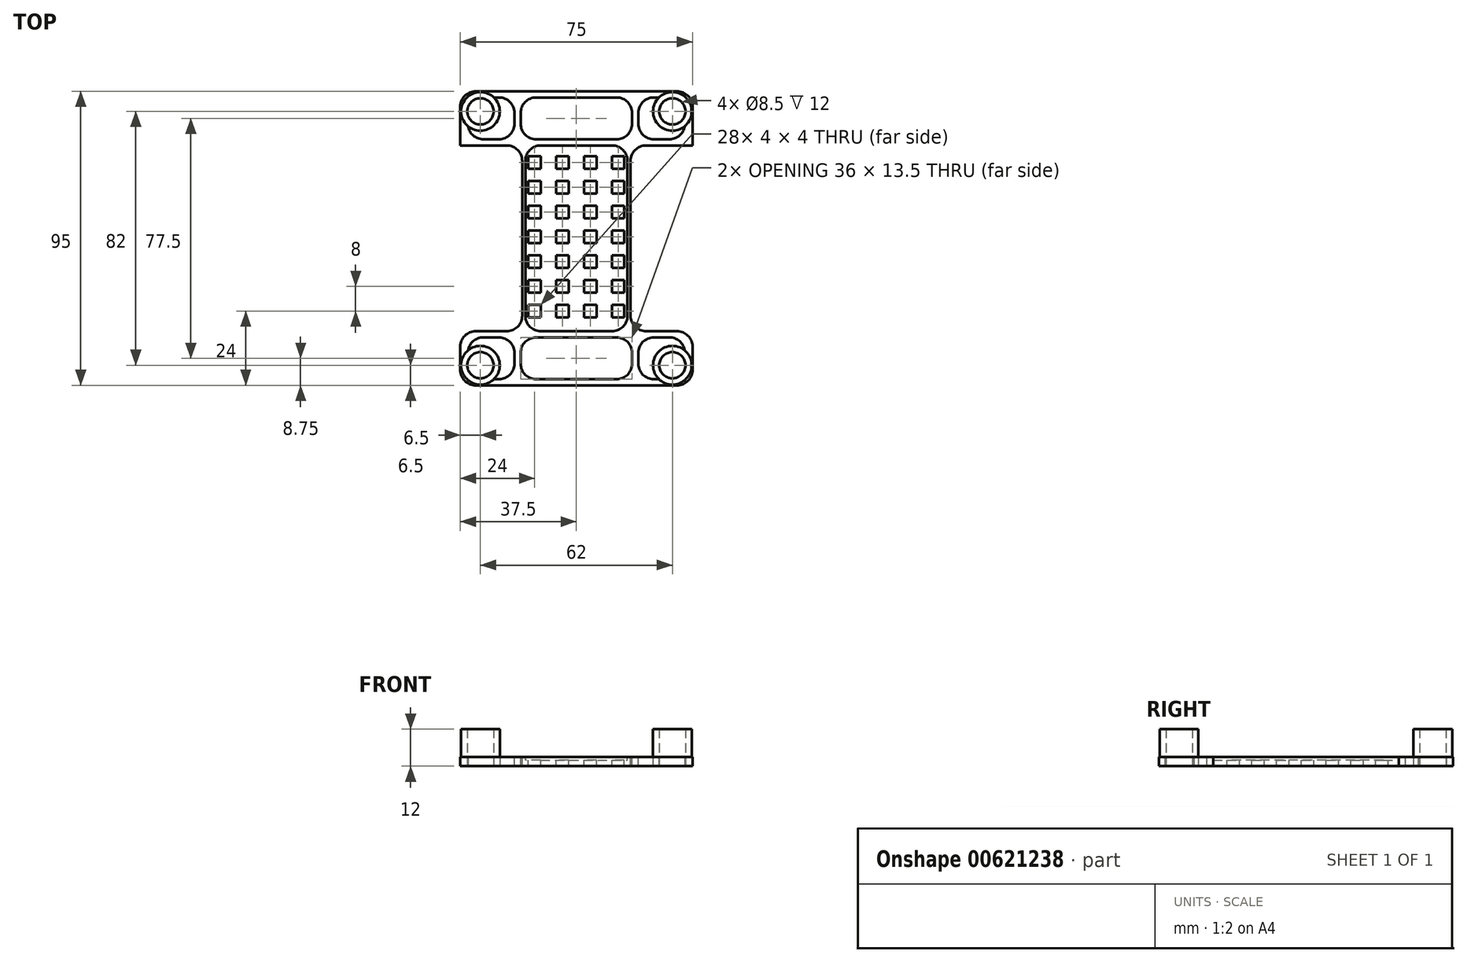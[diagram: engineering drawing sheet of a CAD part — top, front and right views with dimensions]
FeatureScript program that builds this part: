
annotation { "Feature Type Name" : "Feature", "Feature Type Description" : "" }
export const myFeature = defineFeature(function(context is Context, id is Id, definition is map)
    precondition{}
    {
        {
            var Q0;
            Q0=qCreatedBy(makeId("Top.planeOp"),FACE);
            var sketch = newSketch(context, id + "F0", { "sketchPlane" : qUnion([Q0])});
            skLineSegment(sketch, "E0.bottom", {"start": v(-37.5, 47.5) * mm, "end": v(37.5, 47.5) * mm});
            skLineSegment(sketch, "E0.top", {"start": v(-37.5, -47.5) * mm, "end": v(37.5, -47.5) * mm});
            skLineSegment(sketch, "E0.left", {"start": v(-37.5, 47.5) * mm, "end": v(-37.5, -47.5) * mm});
            skLineSegment(sketch, "E0.right", {"start": v(37.5, 47.5) * mm, "end": v(37.5, -47.5) * mm});
            skPoint(sketch, "E0.middle", {"position": v(0, 0) * mm});
            skSolve(sketch);
        }
        {
            var Q0;
            Q0=makeQuery(id+"F0.imprint","IMPRINT",FACE,{"disambiguationData":[TD([[makeQuery(id+"F0.imprint","IMPRINT",EDGE,{"derivedFrom":sQuery(id+"F0.wireOp",EDGE,"E0.bottom")}),-1.0]])]});
            extrude(context, id + "F1", {"entities" : qUnion([Q0]), "depth" : 3 * mm, "offsetDistance" : 25 * mm});
        }
        {
            var Q0;
            Q0=makeQuery(id+"F1.opExtrude","CAP_FACE",FACE,{"disambiguationData":[OSD([sQuery(id+"F0.wireOp",EDGE,"E0.bottom"),sQuery(id+"F0.wireOp",EDGE,"E0.top"),sQuery(id+"F0.wireOp",EDGE,"E0.left"),sQuery(id+"F0.wireOp",EDGE,"E0.right")])],"isStart":false});
            var sketch = newSketch(context, id + "F2", { "sketchPlane" : qUnion([Q0])});
            skLineSegment(sketch, "E1.bottom", {"start": v(-37.5, 30) * mm, "end": v(-17.5, 30) * mm});
            skLineSegment(sketch, "E1.top", {"start": v(-37.5, -30) * mm, "end": v(-17.5, -30) * mm});
            skLineSegment(sketch, "E1.left", {"start": v(-37.5, 30) * mm, "end": v(-37.5, -30) * mm});
            skLineSegment(sketch, "E1.right", {"start": v(-17.5, 30) * mm, "end": v(-17.5, -30) * mm});
            skLineSegment(sketch, "E2.bottom", {"start": v(37.5, 30) * mm, "end": v(17.5, 30) * mm});
            skLineSegment(sketch, "E2.top", {"start": v(37.5, -30) * mm, "end": v(17.5, -30) * mm});
            skLineSegment(sketch, "E2.left", {"start": v(37.5, 30) * mm, "end": v(37.5, -30) * mm});
            skLineSegment(sketch, "E2.right", {"start": v(17.5, 30) * mm, "end": v(17.5, -30) * mm});
            skSolve(sketch);
        }
        {
            var Q0;
            Q0=makeQuery(id+"F2.imprint","IMPRINT",FACE,{"disambiguationData":[TD([[makeQuery(id+"F2.imprint","IMPRINT",EDGE,{"derivedFrom":sQuery(id+"F2.wireOp",EDGE,"E1.bottom")}),-1.0]])]});
            var Q1;
            Q1=makeQuery(id+"F2.imprint","IMPRINT",FACE,{"disambiguationData":[TD([[makeQuery(id+"F2.imprint","IMPRINT",EDGE,{"derivedFrom":sQuery(id+"F2.wireOp",EDGE,"E2.bottom")}),1.0]])]});
            extrude(context, id + "F3", {"entities" : qUnion([Q0, Q1]), "operationType" : NewBodyOperationType.REMOVE, "endBound" : BoundingType.THROUGH_ALL, "oppositeDirection" : true, "depth" : 25 * mm, "offsetDistance" : 25 * mm});
        }
        {
            var Q0;
            Q0=makeQuery(id+"F1.opExtrude","CAP_FACE",FACE,{"disambiguationData":[OSD([sQuery(id+"F0.wireOp",EDGE,"E0.bottom"),sQuery(id+"F0.wireOp",EDGE,"E0.top"),sQuery(id+"F0.wireOp",EDGE,"E0.left"),sQuery(id+"F0.wireOp",EDGE,"E0.right")])],"isStart":false});
            var sketch = newSketch(context, id + "F4", { "sketchPlane" : qUnion([Q0])});
            skLineSegment(sketch, "E3.bottom", {"start": v(-11.5, 22.5) * mm, "end": v(-15.5, 22.5) * mm});
            skLineSegment(sketch, "E3.top", {"start": v(-11.5, 26.5) * mm, "end": v(-15.5, 26.5) * mm});
            skLineSegment(sketch, "E3.left", {"start": v(-11.5, 22.5) * mm, "end": v(-11.5, 26.5) * mm});
            skLineSegment(sketch, "E3.right", {"start": v(-15.5, 22.5) * mm, "end": v(-15.5, 26.5) * mm});
            skPoint(sketch, "E3.middle", {"position": v(-13.5, 24.5) * mm});
            skLineSegment(sketch, "E4.0.1.0", {"start": v(-11.5, 14.5) * mm, "end": v(-11.5, 18.5) * mm});
            skLineSegment(sketch, "E4.0.1.1", {"start": v(-11.5, 14.5) * mm, "end": v(-15.5, 14.5) * mm});
            skLineSegment(sketch, "E4.0.1.2", {"start": v(-11.5, 18.5) * mm, "end": v(-15.5, 18.5) * mm});
            skPoint(sketch, "E4.0.1.3", {"position": v(-13.5, 16.5) * mm});
            skLineSegment(sketch, "E4.0.1.4", {"start": v(-15.5, 14.5) * mm, "end": v(-15.5, 18.5) * mm});
            skLineSegment(sketch, "E4.0.2.0", {"start": v(-11.5, 6.5) * mm, "end": v(-11.5, 10.5) * mm});
            skLineSegment(sketch, "E4.0.2.1", {"start": v(-11.5, 6.5) * mm, "end": v(-15.5, 6.5) * mm});
            skLineSegment(sketch, "E4.0.2.2", {"start": v(-11.5, 10.5) * mm, "end": v(-15.5, 10.5) * mm});
            skPoint(sketch, "E4.0.2.3", {"position": v(-13.5, 8.5) * mm});
            skLineSegment(sketch, "E4.0.2.4", {"start": v(-15.5, 6.5) * mm, "end": v(-15.5, 10.5) * mm});
            skLineSegment(sketch, "E4.0.3.0", {"start": v(-11.5, -1.5) * mm, "end": v(-11.5, 2.5) * mm});
            skLineSegment(sketch, "E4.0.3.1", {"start": v(-11.5, -1.5) * mm, "end": v(-15.5, -1.5) * mm});
            skLineSegment(sketch, "E4.0.3.2", {"start": v(-11.5, 2.5) * mm, "end": v(-15.5, 2.5) * mm});
            skPoint(sketch, "E4.0.3.3", {"position": v(-13.5, 0.5) * mm});
            skLineSegment(sketch, "E4.0.3.4", {"start": v(-15.5, -1.5) * mm, "end": v(-15.5, 2.5) * mm});
            skLineSegment(sketch, "E4.1.0.0", {"start": v(-2.5, 22.5) * mm, "end": v(-2.5, 26.5) * mm});
            skLineSegment(sketch, "E4.1.0.1", {"start": v(-2.5, 22.5) * mm, "end": v(-6.5, 22.5) * mm});
            skLineSegment(sketch, "E4.1.0.2", {"start": v(-2.5, 26.5) * mm, "end": v(-6.5, 26.5) * mm});
            skPoint(sketch, "E4.1.0.3", {"position": v(-4.5, 24.5) * mm});
            skLineSegment(sketch, "E4.1.0.4", {"start": v(-6.5, 22.5) * mm, "end": v(-6.5, 26.5) * mm});
            skLineSegment(sketch, "E4.1.1.0", {"start": v(-2.5, 14.5) * mm, "end": v(-2.5, 18.5) * mm});
            skLineSegment(sketch, "E4.1.1.1", {"start": v(-2.5, 14.5) * mm, "end": v(-6.5, 14.5) * mm});
            skLineSegment(sketch, "E4.1.1.2", {"start": v(-2.5, 18.5) * mm, "end": v(-6.5, 18.5) * mm});
            skPoint(sketch, "E4.1.1.3", {"position": v(-4.5, 16.5) * mm});
            skLineSegment(sketch, "E4.1.1.4", {"start": v(-6.5, 14.5) * mm, "end": v(-6.5, 18.5) * mm});
            skLineSegment(sketch, "E4.1.2.0", {"start": v(-2.5, 6.5) * mm, "end": v(-2.5, 10.5) * mm});
            skLineSegment(sketch, "E4.1.2.1", {"start": v(-2.5, 6.5) * mm, "end": v(-6.5, 6.5) * mm});
            skLineSegment(sketch, "E4.1.2.2", {"start": v(-2.5, 10.5) * mm, "end": v(-6.5, 10.5) * mm});
            skPoint(sketch, "E4.1.2.3", {"position": v(-4.5, 8.5) * mm});
            skLineSegment(sketch, "E4.1.2.4", {"start": v(-6.5, 6.5) * mm, "end": v(-6.5, 10.5) * mm});
            skLineSegment(sketch, "E4.1.3.0", {"start": v(-2.5, -1.5) * mm, "end": v(-2.5, 2.5) * mm});
            skLineSegment(sketch, "E4.1.3.1", {"start": v(-2.5, -1.5) * mm, "end": v(-6.5, -1.5) * mm});
            skLineSegment(sketch, "E4.1.3.2", {"start": v(-2.5, 2.5) * mm, "end": v(-6.5, 2.5) * mm});
            skPoint(sketch, "E4.1.3.3", {"position": v(-4.5, 0.5) * mm});
            skLineSegment(sketch, "E4.1.3.4", {"start": v(-6.5, -1.5) * mm, "end": v(-6.5, 2.5) * mm});
            skLineSegment(sketch, "E4.2.0.0", {"start": v(6.5, 22.5) * mm, "end": v(6.5, 26.5) * mm});
            skLineSegment(sketch, "E4.2.0.1", {"start": v(6.5, 22.5) * mm, "end": v(2.5, 22.5) * mm});
            skLineSegment(sketch, "E4.2.0.2", {"start": v(6.5, 26.5) * mm, "end": v(2.5, 26.5) * mm});
            skPoint(sketch, "E4.2.0.3", {"position": v(4.5, 24.5) * mm});
            skLineSegment(sketch, "E4.2.0.4", {"start": v(2.5, 22.5) * mm, "end": v(2.5, 26.5) * mm});
            skLineSegment(sketch, "E4.2.1.0", {"start": v(6.5, 14.5) * mm, "end": v(6.5, 18.5) * mm});
            skLineSegment(sketch, "E4.2.1.1", {"start": v(6.5, 14.5) * mm, "end": v(2.5, 14.5) * mm});
            skLineSegment(sketch, "E4.2.1.2", {"start": v(6.5, 18.5) * mm, "end": v(2.5, 18.5) * mm});
            skPoint(sketch, "E4.2.1.3", {"position": v(4.5, 16.5) * mm});
            skLineSegment(sketch, "E4.2.1.4", {"start": v(2.5, 14.5) * mm, "end": v(2.5, 18.5) * mm});
            skLineSegment(sketch, "E4.2.2.0", {"start": v(6.5, 6.5) * mm, "end": v(6.5, 10.5) * mm});
            skLineSegment(sketch, "E4.2.2.1", {"start": v(6.5, 6.5) * mm, "end": v(2.5, 6.5) * mm});
            skLineSegment(sketch, "E4.2.2.2", {"start": v(6.5, 10.5) * mm, "end": v(2.5, 10.5) * mm});
            skPoint(sketch, "E4.2.2.3", {"position": v(4.5, 8.5) * mm});
            skLineSegment(sketch, "E4.2.2.4", {"start": v(2.5, 6.5) * mm, "end": v(2.5, 10.5) * mm});
            skLineSegment(sketch, "E4.2.3.0", {"start": v(6.5, -1.5) * mm, "end": v(6.5, 2.5) * mm});
            skLineSegment(sketch, "E4.2.3.1", {"start": v(6.5, -1.5) * mm, "end": v(2.5, -1.5) * mm});
            skLineSegment(sketch, "E4.2.3.2", {"start": v(6.5, 2.5) * mm, "end": v(2.5, 2.5) * mm});
            skPoint(sketch, "E4.2.3.3", {"position": v(4.5, 0.5) * mm});
            skLineSegment(sketch, "E4.2.3.4", {"start": v(2.5, -1.5) * mm, "end": v(2.5, 2.5) * mm});
            skLineSegment(sketch, "E4.direction1", {"start": v(-15.5, 22.5) * mm, "end": v(-6.5, 22.5) * mm, "construction": true});
            skLineSegment(sketch, "E4.direction2", {"start": v(-15.5, 22.5) * mm, "end": v(-15.5, 14.5) * mm, "construction": true});
            skLineSegment(sketch, "E5.0.3.0", {"start": v(15.5, 22.5) * mm, "end": v(15.5, 26.5) * mm});
            skLineSegment(sketch, "E5.3.3.0", {"start": v(15.5, 22.5) * mm, "end": v(11.5, 22.5) * mm});
            skLineSegment(sketch, "E5.6.3.0", {"start": v(15.5, 26.5) * mm, "end": v(11.5, 26.5) * mm});
            skPoint(sketch, "E5.9.3.0", {"position": v(13.5, 24.5) * mm});
            skLineSegment(sketch, "E5.10.3.0", {"start": v(11.5, 22.5) * mm, "end": v(11.5, 26.5) * mm});
            skLineSegment(sketch, "E5.0.3.1", {"start": v(15.5, 14.5) * mm, "end": v(15.5, 18.5) * mm});
            skLineSegment(sketch, "E5.3.3.1", {"start": v(15.5, 14.5) * mm, "end": v(11.5, 14.5) * mm});
            skLineSegment(sketch, "E5.6.3.1", {"start": v(15.5, 18.5) * mm, "end": v(11.5, 18.5) * mm});
            skPoint(sketch, "E5.9.3.1", {"position": v(13.5, 16.5) * mm});
            skLineSegment(sketch, "E5.10.3.1", {"start": v(11.5, 14.5) * mm, "end": v(11.5, 18.5) * mm});
            skLineSegment(sketch, "E5.0.3.2", {"start": v(15.5, 6.5) * mm, "end": v(15.5, 10.5) * mm});
            skLineSegment(sketch, "E5.3.3.2", {"start": v(15.5, 6.5) * mm, "end": v(11.5, 6.5) * mm});
            skLineSegment(sketch, "E5.6.3.2", {"start": v(15.5, 10.5) * mm, "end": v(11.5, 10.5) * mm});
            skPoint(sketch, "E5.9.3.2", {"position": v(13.5, 8.5) * mm});
            skLineSegment(sketch, "E5.10.3.2", {"start": v(11.5, 6.5) * mm, "end": v(11.5, 10.5) * mm});
            skLineSegment(sketch, "E5.0.3.3", {"start": v(15.5, -1.5) * mm, "end": v(15.5, 2.5) * mm});
            skLineSegment(sketch, "E5.3.3.3", {"start": v(15.5, -1.5) * mm, "end": v(11.5, -1.5) * mm});
            skLineSegment(sketch, "E5.6.3.3", {"start": v(15.5, 2.5) * mm, "end": v(11.5, 2.5) * mm});
            skPoint(sketch, "E5.9.3.3", {"position": v(13.5, 0.5) * mm});
            skLineSegment(sketch, "E5.10.3.3", {"start": v(11.5, -1.5) * mm, "end": v(11.5, 2.5) * mm});
            skLineSegment(sketch, "E6.0.0.4", {"start": v(-11.5, -9.5) * mm, "end": v(-11.5, -5.5) * mm});
            skLineSegment(sketch, "E6.3.0.4", {"start": v(-11.5, -9.5) * mm, "end": v(-15.5, -9.5) * mm});
            skLineSegment(sketch, "E6.6.0.4", {"start": v(-11.5, -5.5) * mm, "end": v(-15.5, -5.5) * mm});
            skPoint(sketch, "E6.9.0.4", {"position": v(-13.5, -7.5) * mm});
            skLineSegment(sketch, "E6.10.0.4", {"start": v(-15.5, -9.5) * mm, "end": v(-15.5, -5.5) * mm});
            skLineSegment(sketch, "E6.0.0.5", {"start": v(-11.5, -17.5) * mm, "end": v(-11.5, -13.5) * mm});
            skLineSegment(sketch, "E6.3.0.5", {"start": v(-11.5, -17.5) * mm, "end": v(-15.5, -17.5) * mm});
            skLineSegment(sketch, "E6.6.0.5", {"start": v(-11.5, -13.5) * mm, "end": v(-15.5, -13.5) * mm});
            skPoint(sketch, "E6.9.0.5", {"position": v(-13.5, -15.5) * mm});
            skLineSegment(sketch, "E6.10.0.5", {"start": v(-15.5, -17.5) * mm, "end": v(-15.5, -13.5) * mm});
            skLineSegment(sketch, "E6.0.1.4", {"start": v(-2.5, -9.5) * mm, "end": v(-2.5, -5.5) * mm});
            skLineSegment(sketch, "E6.3.1.4", {"start": v(-2.5, -9.5) * mm, "end": v(-6.5, -9.5) * mm});
            skLineSegment(sketch, "E6.6.1.4", {"start": v(-2.5, -5.5) * mm, "end": v(-6.5, -5.5) * mm});
            skPoint(sketch, "E6.9.1.4", {"position": v(-4.5, -7.5) * mm});
            skLineSegment(sketch, "E6.10.1.4", {"start": v(-6.5, -9.5) * mm, "end": v(-6.5, -5.5) * mm});
            skLineSegment(sketch, "E6.0.1.5", {"start": v(-2.5, -17.5) * mm, "end": v(-2.5, -13.5) * mm});
            skLineSegment(sketch, "E6.3.1.5", {"start": v(-2.5, -17.5) * mm, "end": v(-6.5, -17.5) * mm});
            skLineSegment(sketch, "E6.6.1.5", {"start": v(-2.5, -13.5) * mm, "end": v(-6.5, -13.5) * mm});
            skPoint(sketch, "E6.9.1.5", {"position": v(-4.5, -15.5) * mm});
            skLineSegment(sketch, "E6.10.1.5", {"start": v(-6.5, -17.5) * mm, "end": v(-6.5, -13.5) * mm});
            skLineSegment(sketch, "E6.0.2.4", {"start": v(6.5, -9.5) * mm, "end": v(6.5, -5.5) * mm});
            skLineSegment(sketch, "E6.3.2.4", {"start": v(6.5, -9.5) * mm, "end": v(2.5, -9.5) * mm});
            skLineSegment(sketch, "E6.6.2.4", {"start": v(6.5, -5.5) * mm, "end": v(2.5, -5.5) * mm});
            skPoint(sketch, "E6.9.2.4", {"position": v(4.5, -7.5) * mm});
            skLineSegment(sketch, "E6.10.2.4", {"start": v(2.5, -9.5) * mm, "end": v(2.5, -5.5) * mm});
            skLineSegment(sketch, "E6.0.2.5", {"start": v(6.5, -17.5) * mm, "end": v(6.5, -13.5) * mm});
            skLineSegment(sketch, "E6.3.2.5", {"start": v(6.5, -17.5) * mm, "end": v(2.5, -17.5) * mm});
            skLineSegment(sketch, "E6.6.2.5", {"start": v(6.5, -13.5) * mm, "end": v(2.5, -13.5) * mm});
            skPoint(sketch, "E6.9.2.5", {"position": v(4.5, -15.5) * mm});
            skLineSegment(sketch, "E6.10.2.5", {"start": v(2.5, -17.5) * mm, "end": v(2.5, -13.5) * mm});
            skLineSegment(sketch, "E6.0.3.4", {"start": v(15.5, -9.5) * mm, "end": v(15.5, -5.5) * mm});
            skLineSegment(sketch, "E6.3.3.4", {"start": v(15.5, -9.5) * mm, "end": v(11.5, -9.5) * mm});
            skLineSegment(sketch, "E6.6.3.4", {"start": v(15.5, -5.5) * mm, "end": v(11.5, -5.5) * mm});
            skPoint(sketch, "E6.9.3.4", {"position": v(13.5, -7.5) * mm});
            skLineSegment(sketch, "E6.10.3.4", {"start": v(11.5, -9.5) * mm, "end": v(11.5, -5.5) * mm});
            skLineSegment(sketch, "E6.0.3.5", {"start": v(15.5, -17.5) * mm, "end": v(15.5, -13.5) * mm});
            skLineSegment(sketch, "E6.3.3.5", {"start": v(15.5, -17.5) * mm, "end": v(11.5, -17.5) * mm});
            skLineSegment(sketch, "E6.6.3.5", {"start": v(15.5, -13.5) * mm, "end": v(11.5, -13.5) * mm});
            skPoint(sketch, "E6.9.3.5", {"position": v(13.5, -15.5) * mm});
            skLineSegment(sketch, "E6.10.3.5", {"start": v(11.5, -17.5) * mm, "end": v(11.5, -13.5) * mm});
            skLineSegment(sketch, "E7.0.0.6", {"start": v(-11.5, -25.5) * mm, "end": v(-11.5, -21.5) * mm});
            skLineSegment(sketch, "E7.3.0.6", {"start": v(-11.5, -25.5) * mm, "end": v(-15.5, -25.5) * mm});
            skLineSegment(sketch, "E7.6.0.6", {"start": v(-11.5, -21.5) * mm, "end": v(-15.5, -21.5) * mm});
            skPoint(sketch, "E7.9.0.6", {"position": v(-13.5, -23.5) * mm});
            skLineSegment(sketch, "E7.10.0.6", {"start": v(-15.5, -25.5) * mm, "end": v(-15.5, -21.5) * mm});
            skLineSegment(sketch, "E7.0.1.6", {"start": v(-2.5, -25.5) * mm, "end": v(-2.5, -21.5) * mm});
            skLineSegment(sketch, "E7.3.1.6", {"start": v(-2.5, -25.5) * mm, "end": v(-6.5, -25.5) * mm});
            skLineSegment(sketch, "E7.6.1.6", {"start": v(-2.5, -21.5) * mm, "end": v(-6.5, -21.5) * mm});
            skPoint(sketch, "E7.9.1.6", {"position": v(-4.5, -23.5) * mm});
            skLineSegment(sketch, "E7.10.1.6", {"start": v(-6.5, -25.5) * mm, "end": v(-6.5, -21.5) * mm});
            skLineSegment(sketch, "E7.0.2.6", {"start": v(6.5, -25.5) * mm, "end": v(6.5, -21.5) * mm});
            skLineSegment(sketch, "E7.3.2.6", {"start": v(6.5, -25.5) * mm, "end": v(2.5, -25.5) * mm});
            skLineSegment(sketch, "E7.6.2.6", {"start": v(6.5, -21.5) * mm, "end": v(2.5, -21.5) * mm});
            skPoint(sketch, "E7.9.2.6", {"position": v(4.5, -23.5) * mm});
            skLineSegment(sketch, "E7.10.2.6", {"start": v(2.5, -25.5) * mm, "end": v(2.5, -21.5) * mm});
            skLineSegment(sketch, "E7.0.3.6", {"start": v(15.5, -25.5) * mm, "end": v(15.5, -21.5) * mm});
            skLineSegment(sketch, "E7.3.3.6", {"start": v(15.5, -25.5) * mm, "end": v(11.5, -25.5) * mm});
            skLineSegment(sketch, "E7.6.3.6", {"start": v(15.5, -21.5) * mm, "end": v(11.5, -21.5) * mm});
            skPoint(sketch, "E7.9.3.6", {"position": v(13.5, -23.5) * mm});
            skLineSegment(sketch, "E7.10.3.6", {"start": v(11.5, -25.5) * mm, "end": v(11.5, -21.5) * mm});
            skSolve(sketch);
        }
        {
            var Q0;
            Q0=makeQuery(id+"F4.imprint","IMPRINT",FACE,{"disambiguationData":[TD([[makeQuery(id+"F4.imprint","IMPRINT",EDGE,{"derivedFrom":sQuery(id+"F4.wireOp",EDGE,"E5.0.3.3")}),1.0]])]});
            var Q1;
            Q1=makeQuery(id+"F4.imprint","IMPRINT",FACE,{"disambiguationData":[TD([[makeQuery(id+"F4.imprint","IMPRINT",EDGE,{"derivedFrom":sQuery(id+"F4.wireOp",EDGE,"E5.0.3.1")}),1.0]])]});
            var Q2;
            Q2=makeQuery(id+"F4.imprint","IMPRINT",FACE,{"disambiguationData":[TD([[makeQuery(id+"F4.imprint","IMPRINT",EDGE,{"derivedFrom":sQuery(id+"F4.wireOp",EDGE,"E5.0.3.2")}),1.0]])]});
            var Q3;
            Q3=makeQuery(id+"F4.imprint","IMPRINT",FACE,{"disambiguationData":[TD([[makeQuery(id+"F4.imprint","IMPRINT",EDGE,{"derivedFrom":sQuery(id+"F4.wireOp",EDGE,"E3.bottom")}),-1.0]])]});
            var Q4;
            Q4=makeQuery(id+"F4.imprint","IMPRINT",FACE,{"disambiguationData":[TD([[makeQuery(id+"F4.imprint","IMPRINT",EDGE,{"derivedFrom":sQuery(id+"F4.wireOp",EDGE,"E4.0.1.0")}),1.0]])]});
            var Q5;
            Q5=makeQuery(id+"F4.imprint","IMPRINT",FACE,{"disambiguationData":[TD([[makeQuery(id+"F4.imprint","IMPRINT",EDGE,{"derivedFrom":sQuery(id+"F4.wireOp",EDGE,"E4.0.2.0")}),1.0]])]});
            var Q6;
            Q6=makeQuery(id+"F4.imprint","IMPRINT",FACE,{"disambiguationData":[TD([[makeQuery(id+"F4.imprint","IMPRINT",EDGE,{"derivedFrom":sQuery(id+"F4.wireOp",EDGE,"E4.0.3.0")}),1.0]])]});
            var Q7;
            Q7=makeQuery(id+"F4.imprint","IMPRINT",FACE,{"disambiguationData":[TD([[makeQuery(id+"F4.imprint","IMPRINT",EDGE,{"derivedFrom":sQuery(id+"F4.wireOp",EDGE,"E4.1.0.0")}),1.0]])]});
            var Q8;
            Q8=makeQuery(id+"F4.imprint","IMPRINT",FACE,{"disambiguationData":[TD([[makeQuery(id+"F4.imprint","IMPRINT",EDGE,{"derivedFrom":sQuery(id+"F4.wireOp",EDGE,"E4.1.1.0")}),1.0]])]});
            var Q9;
            Q9=makeQuery(id+"F4.imprint","IMPRINT",FACE,{"disambiguationData":[TD([[makeQuery(id+"F4.imprint","IMPRINT",EDGE,{"derivedFrom":sQuery(id+"F4.wireOp",EDGE,"E4.1.2.0")}),1.0]])]});
            var Q10;
            Q10=makeQuery(id+"F4.imprint","IMPRINT",FACE,{"disambiguationData":[TD([[makeQuery(id+"F4.imprint","IMPRINT",EDGE,{"derivedFrom":sQuery(id+"F4.wireOp",EDGE,"E4.1.3.0")}),1.0]])]});
            var Q11;
            Q11=makeQuery(id+"F4.imprint","IMPRINT",FACE,{"disambiguationData":[TD([[makeQuery(id+"F4.imprint","IMPRINT",EDGE,{"derivedFrom":sQuery(id+"F4.wireOp",EDGE,"E4.2.0.0")}),1.0]])]});
            var Q12;
            Q12=makeQuery(id+"F4.imprint","IMPRINT",FACE,{"disambiguationData":[TD([[makeQuery(id+"F4.imprint","IMPRINT",EDGE,{"derivedFrom":sQuery(id+"F4.wireOp",EDGE,"E4.2.1.0")}),1.0]])]});
            var Q13;
            Q13=makeQuery(id+"F4.imprint","IMPRINT",FACE,{"disambiguationData":[TD([[makeQuery(id+"F4.imprint","IMPRINT",EDGE,{"derivedFrom":sQuery(id+"F4.wireOp",EDGE,"E4.2.3.0")}),1.0]])]});
            var Q14;
            Q14=makeQuery(id+"F4.imprint","IMPRINT",FACE,{"disambiguationData":[TD([[makeQuery(id+"F4.imprint","IMPRINT",EDGE,{"derivedFrom":sQuery(id+"F4.wireOp",EDGE,"E5.0.3.0")}),1.0]])]});
            var Q15;
            Q15=makeQuery(id+"F4.imprint","IMPRINT",FACE,{"disambiguationData":[TD([[makeQuery(id+"F4.imprint","IMPRINT",EDGE,{"derivedFrom":sQuery(id+"F4.wireOp",EDGE,"E4.2.2.0")}),1.0]])]});
            var Q16;
            Q16=makeQuery(id+"F4.imprint","IMPRINT",FACE,{"disambiguationData":[TD([[makeQuery(id+"F4.imprint","IMPRINT",EDGE,{"derivedFrom":sQuery(id+"F4.wireOp",EDGE,"E7.0.3.6")}),1.0]])]});
            var Q17;
            Q17=makeQuery(id+"F4.imprint","IMPRINT",FACE,{"disambiguationData":[TD([[makeQuery(id+"F4.imprint","IMPRINT",EDGE,{"derivedFrom":sQuery(id+"F4.wireOp",EDGE,"E6.0.2.4")}),1.0]])]});
            var Q18;
            Q18=makeQuery(id+"F4.imprint","IMPRINT",FACE,{"disambiguationData":[TD([[makeQuery(id+"F4.imprint","IMPRINT",EDGE,{"derivedFrom":sQuery(id+"F4.wireOp",EDGE,"E6.0.1.5")}),1.0]])]});
            var Q19;
            Q19=makeQuery(id+"F4.imprint","IMPRINT",FACE,{"disambiguationData":[TD([[makeQuery(id+"F4.imprint","IMPRINT",EDGE,{"derivedFrom":sQuery(id+"F4.wireOp",EDGE,"E7.0.1.6")}),1.0]])]});
            var Q20;
            Q20=makeQuery(id+"F4.imprint","IMPRINT",FACE,{"disambiguationData":[TD([[makeQuery(id+"F4.imprint","IMPRINT",EDGE,{"derivedFrom":sQuery(id+"F4.wireOp",EDGE,"E6.0.3.4")}),1.0]])]});
            var Q21;
            Q21=makeQuery(id+"F4.imprint","IMPRINT",FACE,{"disambiguationData":[TD([[makeQuery(id+"F4.imprint","IMPRINT",EDGE,{"derivedFrom":sQuery(id+"F4.wireOp",EDGE,"E6.0.1.4")}),1.0]])]});
            var Q22;
            Q22=makeQuery(id+"F4.imprint","IMPRINT",FACE,{"disambiguationData":[TD([[makeQuery(id+"F4.imprint","IMPRINT",EDGE,{"derivedFrom":sQuery(id+"F4.wireOp",EDGE,"E7.0.0.6")}),1.0]])]});
            var Q23;
            Q23=makeQuery(id+"F4.imprint","IMPRINT",FACE,{"disambiguationData":[TD([[makeQuery(id+"F4.imprint","IMPRINT",EDGE,{"derivedFrom":sQuery(id+"F4.wireOp",EDGE,"E7.0.2.6")}),1.0]])]});
            var Q24;
            Q24=makeQuery(id+"F4.imprint","IMPRINT",FACE,{"disambiguationData":[TD([[makeQuery(id+"F4.imprint","IMPRINT",EDGE,{"derivedFrom":sQuery(id+"F4.wireOp",EDGE,"E6.0.0.5")}),1.0]])]});
            var Q25;
            Q25=makeQuery(id+"F4.imprint","IMPRINT",FACE,{"disambiguationData":[TD([[makeQuery(id+"F4.imprint","IMPRINT",EDGE,{"derivedFrom":sQuery(id+"F4.wireOp",EDGE,"E6.0.0.4")}),1.0]])]});
            var Q26;
            Q26=makeQuery(id+"F4.imprint","IMPRINT",FACE,{"disambiguationData":[TD([[makeQuery(id+"F4.imprint","IMPRINT",EDGE,{"derivedFrom":sQuery(id+"F4.wireOp",EDGE,"E6.0.3.5")}),1.0]])]});
            var Q27;
            Q27=makeQuery(id+"F4.imprint","IMPRINT",FACE,{"disambiguationData":[TD([[makeQuery(id+"F4.imprint","IMPRINT",EDGE,{"derivedFrom":sQuery(id+"F4.wireOp",EDGE,"E6.0.2.5")}),1.0]])]});
            extrude(context, id + "F5", {"entities" : qUnion([Q0, Q1, Q2, Q3, Q4, Q5, Q6, Q7, Q8, Q9, Q10, Q11, Q12, Q13, Q14, Q15, Q16, Q17, Q18, Q19, Q20, Q21, Q22, Q23, Q24, Q25, Q26, Q27]), "operationType" : NewBodyOperationType.REMOVE, "endBound" : BoundingType.THROUGH_ALL, "oppositeDirection" : true, "depth" : 25 * mm, "offsetDistance" : 25 * mm});
        }
        {
            var Q0;
            Q0=makeQuery(id+"F1.opExtrude","CAP_FACE",FACE,{"disambiguationData":[OSD([sQuery(id+"F0.wireOp",EDGE,"E0.bottom"),sQuery(id+"F0.wireOp",EDGE,"E0.top"),sQuery(id+"F0.wireOp",EDGE,"E0.left"),sQuery(id+"F0.wireOp",EDGE,"E0.right")])],"isStart":false});
            var sketch = newSketch(context, id + "F6", { "sketchPlane" : qUnion([Q0])});
            skLineSegment(sketch, "E8.bottom", {"start": v(-35, 45.5) * mm, "end": v(-20, 45.5) * mm});
            skLineSegment(sketch, "E8.top", {"start": v(-35, 32) * mm, "end": v(-20, 32) * mm});
            skLineSegment(sketch, "E8.left", {"start": v(-35, 45.5) * mm, "end": v(-35, 32) * mm});
            skLineSegment(sketch, "E8.right", {"start": v(-20, 45.5) * mm, "end": v(-20, 32) * mm});
            skLineSegment(sketch, "E9.0.1.0", {"start": v(-35, -32) * mm, "end": v(-20, -32) * mm});
            skLineSegment(sketch, "E9.0.1.1", {"start": v(-20, -32) * mm, "end": v(-20, -45.5) * mm});
            skLineSegment(sketch, "E9.0.1.2", {"start": v(-35, -32) * mm, "end": v(-35, -45.5) * mm});
            skLineSegment(sketch, "E9.0.1.3", {"start": v(-35, -45.5) * mm, "end": v(-20, -45.5) * mm});
            skLineSegment(sketch, "E9.1.0.0", {"start": v(20, 45.5) * mm, "end": v(35, 45.5) * mm});
            skLineSegment(sketch, "E9.1.0.1", {"start": v(35, 45.5) * mm, "end": v(35, 32) * mm});
            skLineSegment(sketch, "E9.1.0.2", {"start": v(20, 45.5) * mm, "end": v(20, 32) * mm});
            skLineSegment(sketch, "E9.1.0.3", {"start": v(20, 32) * mm, "end": v(35, 32) * mm});
            skLineSegment(sketch, "E9.1.1.0", {"start": v(20, -32) * mm, "end": v(35, -32) * mm});
            skLineSegment(sketch, "E9.1.1.1", {"start": v(35, -32) * mm, "end": v(35, -45.5) * mm});
            skLineSegment(sketch, "E9.1.1.2", {"start": v(20, -32) * mm, "end": v(20, -45.5) * mm});
            skLineSegment(sketch, "E9.1.1.3", {"start": v(20, -45.5) * mm, "end": v(35, -45.5) * mm});
            skLineSegment(sketch, "E9.direction1", {"start": v(-35, 32) * mm, "end": v(20, 32) * mm, "construction": true});
            skLineSegment(sketch, "E9.direction2", {"start": v(-35, 32) * mm, "end": v(-35, -45.5) * mm, "construction": true});
            skSolve(sketch);
        }
        {
            var Q0;
            Q0=makeQuery(id+"F6.imprint","IMPRINT",FACE,{"disambiguationData":[TD([[makeQuery(id+"F6.imprint","IMPRINT",EDGE,{"derivedFrom":sQuery(id+"F6.wireOp",EDGE,"E8.bottom")}),-1.0]])]});
            var Q1;
            Q1=makeQuery(id+"F6.imprint","IMPRINT",FACE,{"disambiguationData":[TD([[makeQuery(id+"F6.imprint","IMPRINT",EDGE,{"derivedFrom":sQuery(id+"F6.wireOp",EDGE,"E9.1.0.0")}),-1.0]])]});
            var Q2;
            Q2=makeQuery(id+"F6.imprint","IMPRINT",FACE,{"disambiguationData":[TD([[makeQuery(id+"F6.imprint","IMPRINT",EDGE,{"derivedFrom":sQuery(id+"F6.wireOp",EDGE,"E9.0.1.0")}),-1.0]])]});
            var Q3;
            Q3=makeQuery(id+"F6.imprint","IMPRINT",FACE,{"disambiguationData":[TD([[makeQuery(id+"F6.imprint","IMPRINT",EDGE,{"derivedFrom":sQuery(id+"F6.wireOp",EDGE,"E9.1.1.0")}),-1.0]])]});
            extrude(context, id + "F7", {"entities" : qUnion([Q0, Q1, Q2, Q3]), "operationType" : NewBodyOperationType.REMOVE, "endBound" : BoundingType.THROUGH_ALL, "oppositeDirection" : true, "depth" : 25 * mm, "offsetDistance" : 25 * mm});
        }
        {
            var Q0;
            Q0=makeQuery(id+"F1.opExtrude","CAP_FACE",FACE,{"disambiguationData":[OSD([sQuery(id+"F0.wireOp",EDGE,"E0.bottom"),sQuery(id+"F0.wireOp",EDGE,"E0.top"),sQuery(id+"F0.wireOp",EDGE,"E0.left"),sQuery(id+"F0.wireOp",EDGE,"E0.right")])],"isStart":true});
            var sketch = newSketch(context, id + "F8", { "sketchPlane" : qUnion([Q0])});
            skLineSegment(sketch, "E10.bottom", {"start": v(31, -41) * mm, "end": v(-31, -41) * mm, "construction": true});
            skLineSegment(sketch, "E10.top", {"start": v(31, 41) * mm, "end": v(-31, 41) * mm, "construction": true});
            skLineSegment(sketch, "E10.left", {"start": v(31, -41) * mm, "end": v(31, 41) * mm, "construction": true});
            skPoint(sketch, "E10.middle", {"position": v(0, 0) * mm});
            skCircle(sketch, "E11", {"center": v(-31, 41) * mm, "radius": 4.25 * mm});
            skCircle(sketch, "E12", {"center": v(-31, -41) * mm, "radius": 4.25 * mm});
            skCircle(sketch, "E13", {"center": v(31, -41) * mm, "radius": 4.25 * mm});
            skCircle(sketch, "E14", {"center": v(31, 41) * mm, "radius": 4.25 * mm});
            skCircle(sketch, "E15.0", {"center": v(-31, 41) * mm, "radius": 6.25 * mm});
            skCircle(sketch, "E16.0.1.0", {"center": v(-31, -41) * mm, "radius": 6.25 * mm});
            skCircle(sketch, "E16.1.0.0", {"center": v(31, 41) * mm, "radius": 6.25 * mm});
            skCircle(sketch, "E16.1.1.0", {"center": v(31, -41) * mm, "radius": 6.25 * mm});
            skLineSegment(sketch, "E17", {"start": v(-31, 41) * mm, "end": v(-31, -41) * mm, "construction": true});
            skSolve(sketch);
        }
        {
            var Q0;
            {var subQ0=makeQuery(id+"F1.opExtrude","CAP_FACE",FACE,{"disambiguationData":[OSD([sQuery(id+"F0.wireOp",EDGE,"E0.bottom"),sQuery(id+"F0.wireOp",EDGE,"E0.top"),sQuery(id+"F0.wireOp",EDGE,"E0.left"),sQuery(id+"F0.wireOp",EDGE,"E0.right")])],"isStart":true});var subQ1=makeQuery(id+"F7.boolean.opBoolean","INTERSECT",EDGE,{"derivedFrom":[subQ0,makeQuery(id+"F7.opExtrude","SWEPT_FACE",FACE,{"disambiguationData":[OSD([sQuery(id+"F6.wireOp",EDGE,"E8.left")])]})]});var subQ4=sQuery(id+"F8.wireOp",EDGE,"E12");var subQ5=makeQuery(id+"F8.imprint","INTERSECT",VERTEX,{"disambiguationData":[OD(0.0)],"derivedFrom":[subQ1,subQ4]});Q0=makeQuery(id+"F8.imprint","IMPRINT",FACE,{"disambiguationData":[TD([[makeQuery(id+"F8.imprint","IMPRINT",EDGE,{"disambiguationData":[TD([[subQ5,-1.0]])],"derivedFrom":subQ4}),-1.0]])]});}
            var Q1;
            {var subQ0=makeQuery(id+"F1.opExtrude","CAP_FACE",FACE,{"disambiguationData":[OSD([sQuery(id+"F0.wireOp",EDGE,"E0.bottom"),sQuery(id+"F0.wireOp",EDGE,"E0.top"),sQuery(id+"F0.wireOp",EDGE,"E0.left"),sQuery(id+"F0.wireOp",EDGE,"E0.right")])],"isStart":true});var subQ1=makeQuery(id+"F7.boolean.opBoolean","INTERSECT",EDGE,{"derivedFrom":[subQ0,makeQuery(id+"F7.opExtrude","SWEPT_FACE",FACE,{"disambiguationData":[OSD([sQuery(id+"F6.wireOp",EDGE,"E8.left")])]})]});var subQ7=sQuery(id+"F8.wireOp",EDGE,"E12");var subQ8=makeQuery(id+"F8.imprint","INTERSECT",VERTEX,{"disambiguationData":[OD(0.0)],"derivedFrom":[subQ1,subQ7]});Q1=makeQuery(id+"F8.imprint","IMPRINT",FACE,{"disambiguationData":[TD([[makeQuery(id+"F8.imprint","IMPRINT",EDGE,{"disambiguationData":[TD([[subQ8,1.0]])],"derivedFrom":subQ7}),-1.0]])]});}
            var Q2;
            {var subQ0=makeQuery(id+"F1.opExtrude","CAP_FACE",FACE,{"disambiguationData":[OSD([sQuery(id+"F0.wireOp",EDGE,"E0.bottom"),sQuery(id+"F0.wireOp",EDGE,"E0.top"),sQuery(id+"F0.wireOp",EDGE,"E0.left"),sQuery(id+"F0.wireOp",EDGE,"E0.right")])],"isStart":true});var subQ1=makeQuery(id+"F7.boolean.opBoolean","INTERSECT",EDGE,{"derivedFrom":[subQ0,makeQuery(id+"F7.opExtrude","SWEPT_FACE",FACE,{"disambiguationData":[OSD([sQuery(id+"F6.wireOp",EDGE,"E9.1.0.1")])]})]});var subQ4=sQuery(id+"F8.wireOp",EDGE,"E13");var subQ5=makeQuery(id+"F8.imprint","INTERSECT",VERTEX,{"disambiguationData":[OD(0.0)],"derivedFrom":[subQ1,subQ4]});Q2=makeQuery(id+"F8.imprint","IMPRINT",FACE,{"disambiguationData":[TD([[makeQuery(id+"F8.imprint","IMPRINT",EDGE,{"disambiguationData":[TD([[subQ5,1.0]])],"derivedFrom":subQ4}),-1.0]])]});}
            var Q3;
            {var subQ0=makeQuery(id+"F1.opExtrude","CAP_FACE",FACE,{"disambiguationData":[OSD([sQuery(id+"F0.wireOp",EDGE,"E0.bottom"),sQuery(id+"F0.wireOp",EDGE,"E0.top"),sQuery(id+"F0.wireOp",EDGE,"E0.left"),sQuery(id+"F0.wireOp",EDGE,"E0.right")])],"isStart":true});var subQ1=makeQuery(id+"F7.boolean.opBoolean","INTERSECT",EDGE,{"derivedFrom":[subQ0,makeQuery(id+"F7.opExtrude","SWEPT_FACE",FACE,{"disambiguationData":[OSD([sQuery(id+"F6.wireOp",EDGE,"E9.1.0.1")])]})]});var subQ6=sQuery(id+"F8.wireOp",EDGE,"E13");var subQ7=makeQuery(id+"F8.imprint","INTERSECT",VERTEX,{"disambiguationData":[OD(0.0)],"derivedFrom":[subQ1,subQ6]});Q3=makeQuery(id+"F8.imprint","IMPRINT",FACE,{"disambiguationData":[TD([[makeQuery(id+"F8.imprint","IMPRINT",EDGE,{"disambiguationData":[TD([[subQ7,-1.0]])],"derivedFrom":subQ6}),-1.0]])]});}
            var Q4;
            {var subQ0=makeQuery(id+"F1.opExtrude","CAP_FACE",FACE,{"disambiguationData":[OSD([sQuery(id+"F0.wireOp",EDGE,"E0.bottom"),sQuery(id+"F0.wireOp",EDGE,"E0.top"),sQuery(id+"F0.wireOp",EDGE,"E0.left"),sQuery(id+"F0.wireOp",EDGE,"E0.right")])],"isStart":true});var subQ2=makeQuery(id+"F7.boolean.opBoolean","INTERSECT",EDGE,{"derivedFrom":[subQ0,makeQuery(id+"F7.opExtrude","SWEPT_FACE",FACE,{"disambiguationData":[OSD([sQuery(id+"F6.wireOp",EDGE,"E9.1.1.1")])]})]});var subQ6=sQuery(id+"F8.wireOp",EDGE,"E14");var subQ7=makeQuery(id+"F8.imprint","INTERSECT",VERTEX,{"disambiguationData":[OD(0.0)],"derivedFrom":[subQ2,subQ6]});Q4=makeQuery(id+"F8.imprint","IMPRINT",FACE,{"disambiguationData":[TD([[makeQuery(id+"F8.imprint","IMPRINT",EDGE,{"disambiguationData":[TD([[subQ7,-1.0]])],"derivedFrom":subQ6}),-1.0]])]});}
            var Q5;
            {var subQ0=makeQuery(id+"F1.opExtrude","CAP_FACE",FACE,{"disambiguationData":[OSD([sQuery(id+"F0.wireOp",EDGE,"E0.bottom"),sQuery(id+"F0.wireOp",EDGE,"E0.top"),sQuery(id+"F0.wireOp",EDGE,"E0.left"),sQuery(id+"F0.wireOp",EDGE,"E0.right")])],"isStart":true});var subQ2=makeQuery(id+"F7.boolean.opBoolean","INTERSECT",EDGE,{"derivedFrom":[subQ0,makeQuery(id+"F7.opExtrude","SWEPT_FACE",FACE,{"disambiguationData":[OSD([sQuery(id+"F6.wireOp",EDGE,"E9.1.1.1")])]})]});var subQ6=sQuery(id+"F8.wireOp",EDGE,"E14");var subQ7=makeQuery(id+"F8.imprint","INTERSECT",VERTEX,{"disambiguationData":[OD(0.0)],"derivedFrom":[subQ2,subQ6]});Q5=makeQuery(id+"F8.imprint","IMPRINT",FACE,{"disambiguationData":[TD([[makeQuery(id+"F8.imprint","IMPRINT",EDGE,{"disambiguationData":[TD([[subQ7,1.0]])],"derivedFrom":subQ6}),-1.0]])]});}
            var Q6;
            {var subQ0=makeQuery(id+"F1.opExtrude","CAP_FACE",FACE,{"disambiguationData":[OSD([sQuery(id+"F0.wireOp",EDGE,"E0.bottom"),sQuery(id+"F0.wireOp",EDGE,"E0.top"),sQuery(id+"F0.wireOp",EDGE,"E0.left"),sQuery(id+"F0.wireOp",EDGE,"E0.right")])],"isStart":true});var subQ2=makeQuery(id+"F7.boolean.opBoolean","INTERSECT",EDGE,{"derivedFrom":[subQ0,makeQuery(id+"F7.opExtrude","SWEPT_FACE",FACE,{"disambiguationData":[OSD([sQuery(id+"F6.wireOp",EDGE,"E9.0.1.2")])]})]});var subQ7=sQuery(id+"F8.wireOp",EDGE,"E11");var subQ8=makeQuery(id+"F8.imprint","INTERSECT",VERTEX,{"disambiguationData":[OD(0.0)],"derivedFrom":[subQ2,subQ7]});Q6=makeQuery(id+"F8.imprint","IMPRINT",FACE,{"disambiguationData":[TD([[makeQuery(id+"F8.imprint","IMPRINT",EDGE,{"disambiguationData":[TD([[subQ8,-1.0]])],"derivedFrom":subQ7}),-1.0]])]});}
            var Q7;
            {var subQ0=makeQuery(id+"F1.opExtrude","CAP_FACE",FACE,{"disambiguationData":[OSD([sQuery(id+"F0.wireOp",EDGE,"E0.bottom"),sQuery(id+"F0.wireOp",EDGE,"E0.top"),sQuery(id+"F0.wireOp",EDGE,"E0.left"),sQuery(id+"F0.wireOp",EDGE,"E0.right")])],"isStart":true});var subQ2=makeQuery(id+"F7.boolean.opBoolean","INTERSECT",EDGE,{"derivedFrom":[subQ0,makeQuery(id+"F7.opExtrude","SWEPT_FACE",FACE,{"disambiguationData":[OSD([sQuery(id+"F6.wireOp",EDGE,"E9.0.1.2")])]})]});var subQ6=sQuery(id+"F8.wireOp",EDGE,"E11");var subQ7=makeQuery(id+"F8.imprint","INTERSECT",VERTEX,{"disambiguationData":[OD(0.0)],"derivedFrom":[subQ2,subQ6]});Q7=makeQuery(id+"F8.imprint","IMPRINT",FACE,{"disambiguationData":[TD([[makeQuery(id+"F8.imprint","IMPRINT",EDGE,{"disambiguationData":[TD([[subQ7,1.0]])],"derivedFrom":subQ6}),-1.0]])]});}
            var Q8;
            Q8=sQuery(id+"F8.wireOp",EDGE,"E15.0");
            var Q9;
            Q9=sQuery(id+"F8.wireOp",EDGE,"E11");
            extrude(context, id + "F9", {"entities" : qUnion([Q0, Q1, Q2, Q3, Q4, Q5, Q6, Q7]), "operationType" : NewBodyOperationType.ADD, "surfaceEntities" : qUnion([Q8, Q9]), "oppositeDirection" : true, "depth" : 12 * mm, "offsetDistance" : 25 * mm});
        }
        {
            var Q0;
            {var subQ0=sQuery(id+"F0.wireOp",EDGE,"E0.left");var subQ1=sQuery(id+"F0.wireOp",EDGE,"E0.top");var subQ2=sQuery(id+"F0.wireOp",EDGE,"E0.right");var subQ3=sQuery(id+"F0.wireOp",EDGE,"E0.bottom");Q0=makeQuery(id+"F9.boolean.opBoolean","SPLIT",FACE,{"disambiguationData":[TD([makeQuery(id+"F1.opExtrude","SWEPT_FACE",FACE,{"disambiguationData":[OSD([subQ3])]})])],"derivedFrom":makeQuery(id+"F1.opExtrude","CAP_FACE",FACE,{"disambiguationData":[OSD([subQ3,subQ1,subQ0,subQ2])],"isStart":false})});}
            var sketch = newSketch(context, id + "F10", { "sketchPlane" : qUnion([Q0])});
            skLineSegment(sketch, "E18.bottom", {"start": v(18, 45.5) * mm, "end": v(-18, 45.5) * mm});
            skLineSegment(sketch, "E18.top", {"start": v(18, 32) * mm, "end": v(-18, 32) * mm});
            skLineSegment(sketch, "E18.left", {"start": v(18, 45.5) * mm, "end": v(18, 32) * mm});
            skLineSegment(sketch, "E18.right", {"start": v(-18, 45.5) * mm, "end": v(-18, 32) * mm});
            skPoint(sketch, "E18.middle", {"position": v(0, 38.75) * mm});
            skLineSegment(sketch, "E19.MirrorCS", {"start": v(18, -45.5) * mm, "end": v(-18, -45.5) * mm});
            skPoint(sketch, "E20.MirrorP", {"position": v(0, -38.75) * mm});
            skLineSegment(sketch, "E21.MirrorCS", {"start": v(-18, -45.5) * mm, "end": v(-18, -32) * mm});
            skLineSegment(sketch, "E22.MirrorCS", {"start": v(18, -32) * mm, "end": v(-18, -32) * mm});
            skLineSegment(sketch, "E23.MirrorCS", {"start": v(18, -45.5) * mm, "end": v(18, -32) * mm});
            skSolve(sketch);
        }
        {
            var Q0;
            Q0=makeQuery(id+"F10.imprint","IMPRINT",FACE,{"disambiguationData":[TD([[makeQuery(id+"F10.imprint","IMPRINT",EDGE,{"derivedFrom":sQuery(id+"F10.wireOp",EDGE,"E18.bottom")}),1.0]])]});
            var Q1;
            Q1=makeQuery(id+"F10.imprint","IMPRINT",FACE,{"disambiguationData":[TD([[makeQuery(id+"F10.imprint","IMPRINT",EDGE,{"derivedFrom":sQuery(id+"F10.wireOp",EDGE,"E19.MirrorCS")}),-1.0]])]});
            extrude(context, id + "F11", {"entities" : qUnion([Q0, Q1]), "operationType" : NewBodyOperationType.REMOVE, "endBound" : BoundingType.THROUGH_ALL, "oppositeDirection" : true, "depth" : 25 * mm, "offsetDistance" : 25 * mm});
        }
        {
            var Q0;
            Q0=makeQuery(id+"F9.boolean.opBoolean","SPLIT",FACE,{"disambiguationData":[TD([makeQuery(id+"F9.opExtrude","SWEPT_FACE",FACE,{"disambiguationData":[OSD([sQuery(id+"F8.wireOp",EDGE,"E12")])]})])],"derivedFrom":makeQuery(id+"F1.opExtrude","CAP_FACE",FACE,{"disambiguationData":[OSD([sQuery(id+"F0.wireOp",EDGE,"E0.bottom"),sQuery(id+"F0.wireOp",EDGE,"E0.top"),sQuery(id+"F0.wireOp",EDGE,"E0.left"),sQuery(id+"F0.wireOp",EDGE,"E0.right")])],"isStart":false})});
            var Q1;
            Q1=makeQuery(id+"F9.boolean.opBoolean","SPLIT",FACE,{"disambiguationData":[TD([makeQuery(id+"F9.opExtrude","SWEPT_FACE",FACE,{"disambiguationData":[OSD([sQuery(id+"F8.wireOp",EDGE,"E13")])]})])],"derivedFrom":makeQuery(id+"F1.opExtrude","CAP_FACE",FACE,{"disambiguationData":[OSD([sQuery(id+"F0.wireOp",EDGE,"E0.bottom"),sQuery(id+"F0.wireOp",EDGE,"E0.top"),sQuery(id+"F0.wireOp",EDGE,"E0.left"),sQuery(id+"F0.wireOp",EDGE,"E0.right")])],"isStart":false})});
            var Q2;
            Q2=makeQuery(id+"F9.boolean.opBoolean","SPLIT",FACE,{"disambiguationData":[TD([makeQuery(id+"F9.opExtrude","SWEPT_FACE",FACE,{"disambiguationData":[OSD([sQuery(id+"F8.wireOp",EDGE,"E14")])]})])],"derivedFrom":makeQuery(id+"F1.opExtrude","CAP_FACE",FACE,{"disambiguationData":[OSD([sQuery(id+"F0.wireOp",EDGE,"E0.bottom"),sQuery(id+"F0.wireOp",EDGE,"E0.top"),sQuery(id+"F0.wireOp",EDGE,"E0.left"),sQuery(id+"F0.wireOp",EDGE,"E0.right")])],"isStart":false})});
            var Q3;
            Q3=makeQuery(id+"F9.boolean.opBoolean","SPLIT",FACE,{"disambiguationData":[TD([makeQuery(id+"F9.opExtrude","SWEPT_FACE",FACE,{"disambiguationData":[OSD([sQuery(id+"F8.wireOp",EDGE,"E11")])]})])],"derivedFrom":makeQuery(id+"F1.opExtrude","CAP_FACE",FACE,{"disambiguationData":[OSD([sQuery(id+"F0.wireOp",EDGE,"E0.bottom"),sQuery(id+"F0.wireOp",EDGE,"E0.top"),sQuery(id+"F0.wireOp",EDGE,"E0.left"),sQuery(id+"F0.wireOp",EDGE,"E0.right")])],"isStart":false})});
            extrude(context, id + "F12", {"entities" : qUnion([Q0, Q1, Q2, Q3]), "operationType" : NewBodyOperationType.REMOVE, "endBound" : BoundingType.THROUGH_ALL, "oppositeDirection" : true, "depth" : 25 * mm, "offsetDistance" : 25 * mm});
        }
        {
            var Q0;
            Q0=makeQuery(id+"F1.opExtrude","SWEPT_EDGE",EDGE,{"disambiguationData":[OSD([sQuery(id+"F0.wireOp",EDGE,"E0.top"),sQuery(id+"F0.wireOp",EDGE,"E0.left")])]});
            var Q1;
            Q1=makeQuery(id+"F3.boolean.opBoolean","COPY",EDGE,{"derivedFrom":makeQuery(id+"F3.opExtrude","SWEPT_EDGE",EDGE,{"disambiguationData":[OSD([sQuery(id+"F0.wireOp",EDGE,"E0.left"),sQuery(id+"F2.wireOp",EDGE,"E1.top"),sQuery(id+"F2.wireOp",EDGE,"E1.left")])]})});
            var Q2;
            Q2=makeQuery(id+"F7.boolean.opBoolean","COPY",EDGE,{"derivedFrom":makeQuery(id+"F7.opExtrude","SWEPT_EDGE",EDGE,{"disambiguationData":[OSD([sQuery(id+"F6.wireOp",EDGE,"E9.0.1.0"),sQuery(id+"F6.wireOp",EDGE,"E9.0.1.2")])]})});
            var Q3;
            Q3=makeQuery(id+"F7.boolean.opBoolean","COPY",EDGE,{"derivedFrom":makeQuery(id+"F7.opExtrude","SWEPT_EDGE",EDGE,{"disambiguationData":[OSD([sQuery(id+"F6.wireOp",EDGE,"E9.0.1.0"),sQuery(id+"F6.wireOp",EDGE,"E9.0.1.1")])]})});
            var Q4;
            Q4=makeQuery(id+"F7.boolean.opBoolean","COPY",EDGE,{"derivedFrom":makeQuery(id+"F7.opExtrude","SWEPT_EDGE",EDGE,{"disambiguationData":[OSD([sQuery(id+"F6.wireOp",EDGE,"E9.0.1.1"),sQuery(id+"F6.wireOp",EDGE,"E9.0.1.3")])]})});
            var Q5;
            Q5=makeQuery(id+"F11.boolean.opBoolean","COPY",EDGE,{"derivedFrom":makeQuery(id+"F11.opExtrude","SWEPT_EDGE",EDGE,{"disambiguationData":[OSD([sQuery(id+"F10.wireOp",EDGE,"E21.MirrorCS"),sQuery(id+"F10.wireOp",EDGE,"E22.MirrorCS")])]})});
            var Q6;
            Q6=makeQuery(id+"F11.boolean.opBoolean","COPY",EDGE,{"derivedFrom":makeQuery(id+"F11.opExtrude","SWEPT_EDGE",EDGE,{"disambiguationData":[OSD([sQuery(id+"F10.wireOp",EDGE,"E19.MirrorCS"),sQuery(id+"F10.wireOp",EDGE,"E21.MirrorCS")])]})});
            var Q7;
            Q7=makeQuery(id+"F11.boolean.opBoolean","COPY",EDGE,{"derivedFrom":makeQuery(id+"F11.opExtrude","SWEPT_EDGE",EDGE,{"disambiguationData":[OSD([sQuery(id+"F10.wireOp",EDGE,"E19.MirrorCS"),sQuery(id+"F10.wireOp",EDGE,"E23.MirrorCS")])]})});
            var Q8;
            Q8=makeQuery(id+"F11.boolean.opBoolean","COPY",EDGE,{"derivedFrom":makeQuery(id+"F11.opExtrude","SWEPT_EDGE",EDGE,{"disambiguationData":[OSD([sQuery(id+"F10.wireOp",EDGE,"E22.MirrorCS"),sQuery(id+"F10.wireOp",EDGE,"E23.MirrorCS")])]})});
            var Q9;
            Q9=makeQuery(id+"F7.boolean.opBoolean","COPY",EDGE,{"derivedFrom":makeQuery(id+"F7.opExtrude","SWEPT_EDGE",EDGE,{"disambiguationData":[OSD([sQuery(id+"F6.wireOp",EDGE,"E9.1.1.0"),sQuery(id+"F6.wireOp",EDGE,"E9.1.1.2")])]})});
            var Q10;
            Q10=makeQuery(id+"F7.boolean.opBoolean","COPY",EDGE,{"derivedFrom":makeQuery(id+"F7.opExtrude","SWEPT_EDGE",EDGE,{"disambiguationData":[OSD([sQuery(id+"F6.wireOp",EDGE,"E9.1.1.2"),sQuery(id+"F6.wireOp",EDGE,"E9.1.1.3")])]})});
            var Q11;
            Q11=makeQuery(id+"F7.boolean.opBoolean","COPY",EDGE,{"derivedFrom":makeQuery(id+"F7.opExtrude","SWEPT_EDGE",EDGE,{"disambiguationData":[OSD([sQuery(id+"F6.wireOp",EDGE,"E9.1.1.0"),sQuery(id+"F6.wireOp",EDGE,"E9.1.1.1")])]})});
            var Q12;
            Q12=makeQuery(id+"F1.opExtrude","SWEPT_EDGE",EDGE,{"disambiguationData":[OSD([sQuery(id+"F0.wireOp",EDGE,"E0.top"),sQuery(id+"F0.wireOp",EDGE,"E0.right")])]});
            var Q13;
            Q13=makeQuery(id+"F3.boolean.opBoolean","COPY",EDGE,{"derivedFrom":makeQuery(id+"F3.opExtrude","SWEPT_EDGE",EDGE,{"disambiguationData":[OSD([sQuery(id+"F0.wireOp",EDGE,"E0.right"),sQuery(id+"F2.wireOp",EDGE,"E2.top"),sQuery(id+"F2.wireOp",EDGE,"E2.left")])]})});
            var Q14;
            Q14=makeQuery(id+"F1.opExtrude","SWEPT_EDGE",EDGE,{"disambiguationData":[OSD([sQuery(id+"F0.wireOp",EDGE,"E0.bottom"),sQuery(id+"F0.wireOp",EDGE,"E0.left")])]});
            var Q15;
            Q15=makeQuery(id+"F3.boolean.opBoolean","COPY",EDGE,{"derivedFrom":makeQuery(id+"F3.opExtrude","SWEPT_EDGE",EDGE,{"disambiguationData":[OSD([sQuery(id+"F0.wireOp",EDGE,"E0.left"),sQuery(id+"F2.wireOp",EDGE,"E1.bottom"),sQuery(id+"F2.wireOp",EDGE,"E1.left")])]})});
            var Q16;
            Q16=makeQuery(id+"F7.boolean.opBoolean","COPY",EDGE,{"derivedFrom":makeQuery(id+"F7.opExtrude","SWEPT_EDGE",EDGE,{"disambiguationData":[OSD([sQuery(id+"F6.wireOp",EDGE,"E8.bottom"),sQuery(id+"F6.wireOp",EDGE,"E8.right")])]})});
            var Q17;
            Q17=makeQuery(id+"F7.boolean.opBoolean","COPY",EDGE,{"derivedFrom":makeQuery(id+"F7.opExtrude","SWEPT_EDGE",EDGE,{"disambiguationData":[OSD([sQuery(id+"F6.wireOp",EDGE,"E8.top"),sQuery(id+"F6.wireOp",EDGE,"E8.right")])]})});
            var Q18;
            Q18=makeQuery(id+"F7.boolean.opBoolean","COPY",EDGE,{"derivedFrom":makeQuery(id+"F7.opExtrude","SWEPT_EDGE",EDGE,{"disambiguationData":[OSD([sQuery(id+"F6.wireOp",EDGE,"E8.top"),sQuery(id+"F6.wireOp",EDGE,"E8.left")])]})});
            var Q19;
            Q19=makeQuery(id+"F11.boolean.opBoolean","COPY",EDGE,{"derivedFrom":makeQuery(id+"F11.opExtrude","SWEPT_EDGE",EDGE,{"disambiguationData":[OSD([sQuery(id+"F10.wireOp",EDGE,"E18.top"),sQuery(id+"F10.wireOp",EDGE,"E18.right")])]})});
            var Q20;
            Q20=makeQuery(id+"F11.boolean.opBoolean","COPY",EDGE,{"derivedFrom":makeQuery(id+"F11.opExtrude","SWEPT_EDGE",EDGE,{"disambiguationData":[OSD([sQuery(id+"F10.wireOp",EDGE,"E18.bottom"),sQuery(id+"F10.wireOp",EDGE,"E18.right")])]})});
            var Q21;
            Q21=makeQuery(id+"F11.boolean.opBoolean","COPY",EDGE,{"derivedFrom":makeQuery(id+"F11.opExtrude","SWEPT_EDGE",EDGE,{"disambiguationData":[OSD([sQuery(id+"F10.wireOp",EDGE,"E18.top"),sQuery(id+"F10.wireOp",EDGE,"E18.left")])]})});
            var Q22;
            Q22=makeQuery(id+"F11.boolean.opBoolean","COPY",EDGE,{"derivedFrom":makeQuery(id+"F11.opExtrude","SWEPT_EDGE",EDGE,{"disambiguationData":[OSD([sQuery(id+"F10.wireOp",EDGE,"E18.bottom"),sQuery(id+"F10.wireOp",EDGE,"E18.left")])]})});
            var Q23;
            Q23=makeQuery(id+"F7.boolean.opBoolean","COPY",EDGE,{"derivedFrom":makeQuery(id+"F7.opExtrude","SWEPT_EDGE",EDGE,{"disambiguationData":[OSD([sQuery(id+"F6.wireOp",EDGE,"E9.1.0.1"),sQuery(id+"F6.wireOp",EDGE,"E9.1.0.3")])]})});
            var Q24;
            Q24=makeQuery(id+"F7.boolean.opBoolean","COPY",EDGE,{"derivedFrom":makeQuery(id+"F7.opExtrude","SWEPT_EDGE",EDGE,{"disambiguationData":[OSD([sQuery(id+"F6.wireOp",EDGE,"E9.1.0.2"),sQuery(id+"F6.wireOp",EDGE,"E9.1.0.3")])]})});
            var Q25;
            Q25=makeQuery(id+"F7.boolean.opBoolean","COPY",EDGE,{"derivedFrom":makeQuery(id+"F7.opExtrude","SWEPT_EDGE",EDGE,{"disambiguationData":[OSD([sQuery(id+"F6.wireOp",EDGE,"E9.1.0.0"),sQuery(id+"F6.wireOp",EDGE,"E9.1.0.2")])]})});
            var Q26;
            Q26=makeQuery(id+"F1.opExtrude","SWEPT_EDGE",EDGE,{"disambiguationData":[OSD([sQuery(id+"F0.wireOp",EDGE,"E0.bottom"),sQuery(id+"F0.wireOp",EDGE,"E0.right")])]});
            var Q27;
            Q27=makeQuery(id+"F3.boolean.opBoolean","COPY",EDGE,{"derivedFrom":makeQuery(id+"F3.opExtrude","SWEPT_EDGE",EDGE,{"disambiguationData":[OSD([sQuery(id+"F0.wireOp",EDGE,"E0.right"),sQuery(id+"F2.wireOp",EDGE,"E2.bottom"),sQuery(id+"F2.wireOp",EDGE,"E2.left")])]})});
            var Q28;
            Q28=makeQuery(id+"F3.boolean.opBoolean","COPY",EDGE,{"derivedFrom":makeQuery(id+"F3.opExtrude","SWEPT_EDGE",EDGE,{"disambiguationData":[OSD([sQuery(id+"F2.wireOp",EDGE,"E2.bottom"),sQuery(id+"F2.wireOp",EDGE,"E2.right")])]})});
            var Q29;
            Q29=makeQuery(id+"F3.boolean.opBoolean","COPY",EDGE,{"derivedFrom":makeQuery(id+"F3.opExtrude","SWEPT_EDGE",EDGE,{"disambiguationData":[OSD([sQuery(id+"F2.wireOp",EDGE,"E1.bottom"),sQuery(id+"F2.wireOp",EDGE,"E1.right")])]})});
            var Q30;
            Q30=makeQuery(id+"F3.boolean.opBoolean","COPY",EDGE,{"derivedFrom":makeQuery(id+"F3.opExtrude","SWEPT_EDGE",EDGE,{"disambiguationData":[OSD([sQuery(id+"F2.wireOp",EDGE,"E2.top"),sQuery(id+"F2.wireOp",EDGE,"E2.right")])]})});
            var Q31;
            Q31=makeQuery(id+"F3.boolean.opBoolean","COPY",EDGE,{"derivedFrom":makeQuery(id+"F3.opExtrude","SWEPT_EDGE",EDGE,{"disambiguationData":[OSD([sQuery(id+"F2.wireOp",EDGE,"E1.top"),sQuery(id+"F2.wireOp",EDGE,"E1.right")])]})});
            fillet(context, id + "F13", {"entities" : qUnion([Q0, Q1, Q2, Q3, Q4, Q5, Q6, Q7, Q8, Q9, Q10, Q11, Q12, Q13, Q14, Q15, Q16, Q17, Q18, Q19, Q20, Q21, Q22, Q23, Q24, Q25, Q26, Q27, Q28, Q29, Q30, Q31]), "radius" : 5 * mm, "tangentPropagation" : true, "allowEdgeOverflow" : false});
        }
        {
            var Q0;
            {var subQ0=sQuery(id+"F0.wireOp",EDGE,"E0.left");var subQ1=sQuery(id+"F0.wireOp",EDGE,"E0.top");var subQ2=sQuery(id+"F0.wireOp",EDGE,"E0.right");var subQ3=sQuery(id+"F0.wireOp",EDGE,"E0.bottom");Q0=makeQuery(id+"F9.boolean.opBoolean","SPLIT",FACE,{"disambiguationData":[TD([makeQuery(id+"F1.opExtrude","SWEPT_FACE",FACE,{"disambiguationData":[OSD([subQ3])]})])],"derivedFrom":makeQuery(id+"F1.opExtrude","CAP_FACE",FACE,{"disambiguationData":[OSD([subQ3,subQ1,subQ0,subQ2])],"isStart":false})});}
            var sketch = newSketch(context, id + "F14", { "sketchPlane" : qUnion([Q0])});
            skLineSegment(sketch, "E24.bottom", {"start": v(-16.5, 30) * mm, "end": v(16.5, 30) * mm});
            skLineSegment(sketch, "E24.top", {"start": v(-16.5, -30) * mm, "end": v(16.5, -30) * mm});
            skLineSegment(sketch, "E24.left", {"start": v(-16.5, 30) * mm, "end": v(-16.5, -30) * mm});
            skLineSegment(sketch, "E24.right", {"start": v(16.5, 30) * mm, "end": v(16.5, -30) * mm});
            skPoint(sketch, "E24.middle", {"position": v(0, 0) * mm});
            skSolve(sketch);
        }
        {
            var Q0;
            Q0=makeQuery(id+"F14.imprint","IMPRINT",FACE,{"disambiguationData":[TD([[makeQuery(id+"F14.imprint","IMPRINT",EDGE,{"derivedFrom":sQuery(id+"F14.wireOp",EDGE,"E24.bottom")}),-1.0]])]});
            extrude(context, id + "F15", {"entities" : qUnion([Q0]), "operationType" : NewBodyOperationType.REMOVE, "oppositeDirection" : true, "depth" : 1 * mm, "offsetDistance" : 25 * mm});
        }
        {
            var Q0;
            Q0=makeQuery(id+"F15.boolean.opBoolean","COPY",EDGE,{"derivedFrom":makeQuery(id+"F15.opExtrude","SWEPT_EDGE",EDGE,{"disambiguationData":[OSD([sQuery(id+"F14.wireOp",EDGE,"E24.bottom"),sQuery(id+"F14.wireOp",EDGE,"E24.left")])]})});
            var Q1;
            Q1=makeQuery(id+"F15.boolean.opBoolean","COPY",EDGE,{"derivedFrom":makeQuery(id+"F15.opExtrude","SWEPT_EDGE",EDGE,{"disambiguationData":[OSD([sQuery(id+"F14.wireOp",EDGE,"E24.bottom"),sQuery(id+"F14.wireOp",EDGE,"E24.right")])]})});
            var Q2;
            Q2=makeQuery(id+"F15.boolean.opBoolean","COPY",EDGE,{"derivedFrom":makeQuery(id+"F15.opExtrude","SWEPT_EDGE",EDGE,{"disambiguationData":[OSD([sQuery(id+"F14.wireOp",EDGE,"E24.top"),sQuery(id+"F14.wireOp",EDGE,"E24.left")])]})});
            var Q3;
            Q3=makeQuery(id+"F15.boolean.opBoolean","COPY",EDGE,{"derivedFrom":makeQuery(id+"F15.opExtrude","SWEPT_EDGE",EDGE,{"disambiguationData":[OSD([sQuery(id+"F14.wireOp",EDGE,"E24.top"),sQuery(id+"F14.wireOp",EDGE,"E24.right")])]})});
            fillet(context, id + "F16", {"entities" : qUnion([Q0, Q1, Q2, Q3]), "radius" : 5 * mm, "tangentPropagation" : true, "allowEdgeOverflow" : false});
        }
    });
